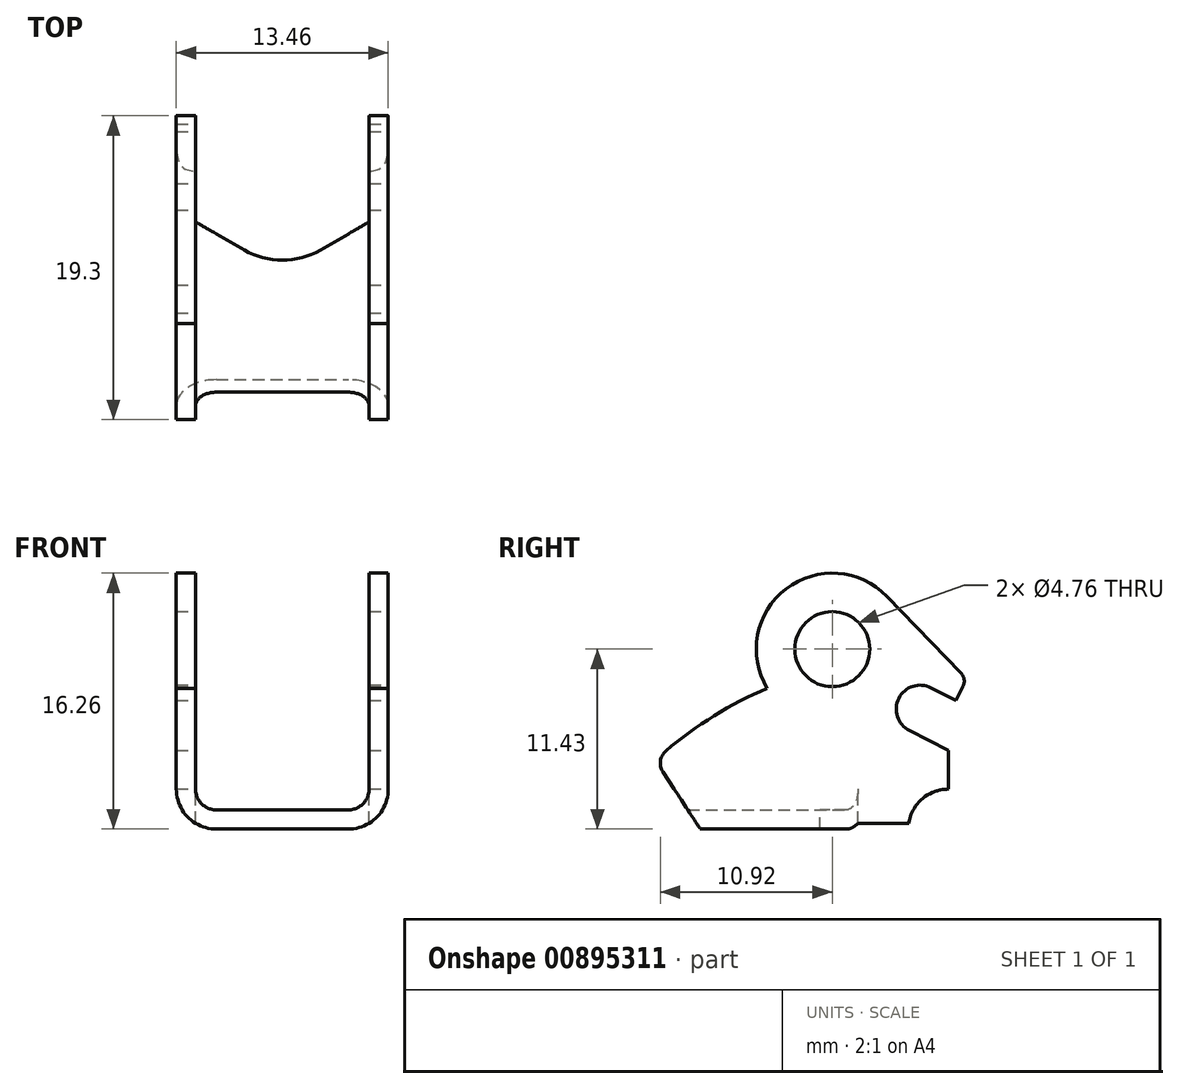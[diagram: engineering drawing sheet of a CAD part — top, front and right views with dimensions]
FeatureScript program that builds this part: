
annotation { "Feature Type Name" : "Feature", "Feature Type Description" : "" }
export const myFeature = defineFeature(function(context is Context, id is Id, definition is map)
    precondition{}
    {
        {
            var Q0;
            Q0=qCreatedBy(makeId("Front.planeOp"),FACE);
            var sketch = newSketch(context, id + "F0", { "sketchPlane" : qUnion([Q0])});
            skLineSegment(sketch, "E0.top", {"start": v(-4.2, 0) * mm, "end": v(4.2, 0) * mm});
            skLineSegment(sketch, "E0.left", {"start": v(-6.73, 25.4) * mm, "end": v(-6.73, 2.54) * mm});
            skLineSegment(sketch, "E0.right", {"start": v(6.73, 25.4) * mm, "end": v(6.73, 2.54) * mm});
            skPoint(sketch, "E1.visualSharp", {"position": v(-6.73, 0) * mm});
            skArc(sketch, "E1.filletArc", {"start": v(-6.73, 2.54) * mm, "mid": v(-5.99, 0.74) * mm, "end": v(-4.2, 0) * mm});
            skPoint(sketch, "E2.visualSharp", {"position": v(6.73, 0) * mm});
            skArc(sketch, "E2.filletArc", {"start": v(4.2, 0) * mm, "mid": v(5.99, 0.74) * mm, "end": v(6.73, 2.54) * mm});
            skLineSegment(sketch, "E3.0", {"start": v(5.51, 25.4) * mm, "end": v(5.51, 2.54) * mm});
            skLineSegment(sketch, "E3.1", {"start": v(-5.51, 25.4) * mm, "end": v(-5.51, 2.54) * mm});
            skArc(sketch, "E3.2", {"start": v(-5.51, 2.54) * mm, "mid": v(-5.12, 1.6) * mm, "end": v(-4.2, 1.22) * mm});
            skLineSegment(sketch, "E3.3", {"start": v(-4.2, 1.22) * mm, "end": v(4.2, 1.22) * mm});
            skArc(sketch, "E3.4", {"start": v(4.2, 1.22) * mm, "mid": v(5.12, 1.6) * mm, "end": v(5.51, 2.54) * mm});
            skLineSegment(sketch, "E4", {"start": v(-6.73, 25.4) * mm, "end": v(-5.51, 25.4) * mm});
            skLineSegment(sketch, "E5", {"start": v(5.51, 25.4) * mm, "end": v(6.73, 25.4) * mm});
            skSolve(sketch);
        }
        {
            var Q0;
            Q0 = qSketchRegion(id + "F0", true);
            extrude(context, id + "F1", {"entities" : qUnion([Q0]), "endBound" : BoundingType.SYMMETRIC, "depth" : 25.4 * mm, "offsetDistance" : 25.4 * mm});
        }
        {
            var Q0;
            Q0=qCreatedBy(makeId("Right.planeOp"),FACE);
            var sketch = newSketch(context, id + "F2", { "sketchPlane" : qUnion([Q0])});
            skLineSegment(sketch, "E6", {"start": v(-20, 11.43) * mm, "end": v(20.9, 11.43) * mm, "construction": true});
            skLineSegment(sketch, "E7", {"start": v(-9.9, 27.47) * mm, "end": v(-9.9, -7.2) * mm, "construction": true});
            skLineSegment(sketch, "E8", {"start": v(5.59, 5.39) * mm, "end": v(5.59, -18.34) * mm, "construction": true});
            skLineSegment(sketch, "E9", {"start": v(-18.82, -13.97) * mm, "end": v(26.6, -13.97) * mm, "construction": true});
            skLineSegment(sketch, "E10", {"start": v(-23.18, 4.2) * mm, "end": v(8.59, 4.2) * mm, "construction": true});
            skCircle(sketch, "E11", {"center": v(-9.9, 4.2) * mm, "radius": 1.02 * mm, "construction": true});
            skLineSegment(sketch, "E12", {"start": v(-8.38, 6.18) * mm, "end": v(-8.38, -4.98) * mm, "construction": true});
            skLineSegment(sketch, "E13", {"start": v(-8.38, 0) * mm, "end": v(-10.76, 3.64) * mm});
            skLineSegment(sketch, "E14", {"start": v(0, 15.75) * mm, "end": v(0, -4.51) * mm, "construction": true});
            skArc(sketch, "E15", {"start": v(-10.57, 4.97) * mm, "mid": v(-10.91, 4.34) * mm, "end": v(-10.76, 3.64) * mm});
            skPoint(sketch, "E16", {"position": v(-8.09, 6.83) * mm});
            skArc(sketch, "E17", {"start": v(-4.14, 8.94) * mm, "mid": v(-7.5, 7.2) * mm, "end": v(-10.57, 4.97) * mm});
            skCircle(sketch, "E18", {"center": v(0, 11.43) * mm, "radius": 2.38 * mm});
            skLineSegment(sketch, "E19", {"start": v(5.59, 15.52) * mm, "end": v(5.59, 7.4) * mm, "construction": true});
            skLineSegment(sketch, "E20", {"start": v(7.62, 15.4) * mm, "end": v(7.62, 6.54) * mm, "construction": true});
            skLineSegment(sketch, "E21", {"start": v(9.97, 9.4) * mm, "end": v(2.43, 9.4) * mm, "construction": true});
            skLineSegment(sketch, "E22", {"start": v(3.47, 14.79) * mm, "end": v(8.17, 9.93) * mm});
            skArc(sketch, "E23", {"start": v(3.47, 14.79) * mm, "mid": v(-2.94, 15.26) * mm, "end": v(-4.14, 8.94) * mm});
            skLineSegment(sketch, "E24", {"start": v(13.77, 7.62) * mm, "end": v(4.28, 7.62) * mm, "construction": true});
            skLineSegment(sketch, "E25", {"start": v(4.9, 6.26) * mm, "end": v(8.4, 4.48) * mm, "construction": true});
            skArc(sketch, "E26", {"start": v(8.3, 9.05) * mm, "mid": v(8.37, 9.51) * mm, "end": v(8.17, 9.93) * mm});
            skLineSegment(sketch, "E27", {"start": v(8.3, 9.05) * mm, "end": v(7.85, 8.18) * mm});
            skLineSegment(sketch, "E28", {"start": v(7.85, 8.18) * mm, "end": v(6.28, 8.98) * mm});
            skArc(sketch, "E29", {"start": v(6.28, 8.98) * mm, "mid": v(4.23, 8.31) * mm, "end": v(4.9, 6.26) * mm});
            skLineSegment(sketch, "E30", {"start": v(4.9, 6.26) * mm, "end": v(7.37, 5) * mm});
            skLineSegment(sketch, "E31", {"start": v(14.66, 2.54) * mm, "end": v(3.5, 2.54) * mm, "construction": true});
            skLineSegment(sketch, "E32", {"start": v(7.37, 5) * mm, "end": v(7.37, 2.54) * mm, "construction": true});
            skArc(sketch, "E33", {"start": v(7.37, 2.54) * mm, "mid": v(5.57, 1.8) * mm, "end": v(4.83, 0) * mm});
            skLineSegment(sketch, "E34", {"start": v(7.37, 5) * mm, "end": v(7.37, 2.54) * mm});
            skLineSegment(sketch, "E35", {"start": v(4.83, 0) * mm, "end": v(-8.38, 0) * mm});
            skSolve(sketch);
        }
        {
            var Q0;
            Q0 = qSketchRegion(id + "F2", true);
            extrude(context, id + "F3", {"entities" : qUnion([Q0]), "operationType" : NewBodyOperationType.INTERSECT, "endBound" : BoundingType.SYMMETRIC, "oppositeDirection" : true, "depth" : 50.8 * mm, "offsetDistance" : 25.4 * mm});
        }
        {
            var Q0;
            Q0=qCreatedBy(makeId("Top.planeOp"),FACE);
            var sketch = newSketch(context, id + "F4", { "sketchPlane" : qUnion([Q0])});
            skLineSegment(sketch, "E36.0", {"start": v(4.2, -9.18) * mm, "end": v(-4.2, -9.18) * mm, "construction": true});
            skLineSegment(sketch, "E37", {"start": v(-9.3, -0.8) * mm, "end": v(11.54, -0.8) * mm, "construction": true});
            skCircle(sketch, "E38", {"center": v(0, 4.03) * mm, "radius": 4.83 * mm, "construction": true});
            skLineSegment(sketch, "E39", {"start": v(10.52, 4.53) * mm, "end": v(-1.79, -2.57) * mm, "construction": true});
            skLineSegment(sketch, "E40", {"start": v(-8, 3.08) * mm, "end": v(2.5, -2.99) * mm});
            skLineSegment(sketch, "E41.0", {"start": v(5.51, 3.47) * mm, "end": v(5.51, -4.83) * mm});
            skLineSegment(sketch, "E41.1", {"start": v(-5.51, 3.47) * mm, "end": v(-5.51, -4.83) * mm});
            skLineSegment(sketch, "E42", {"start": v(-5.51, 1.64) * mm, "end": v(-2.67, 0) * mm});
            skLineSegment(sketch, "E43", {"start": v(5.51, 1.64) * mm, "end": v(5.51, 11.05) * mm});
            skLineSegment(sketch, "E44", {"start": v(5.51, 11.05) * mm, "end": v(-5.51, 11.05) * mm});
            skLineSegment(sketch, "E45", {"start": v(-5.51, 11.05) * mm, "end": v(-5.51, 1.64) * mm});
            skLineSegment(sketch, "E46", {"start": v(5.51, 1.64) * mm, "end": v(2.41, -0.15) * mm});
            skArc(sketch, "E47", {"start": v(-2.65, 0) * mm, "mid": v(-0.14, -0.8) * mm, "end": v(2.41, -0.15) * mm});
            skSolve(sketch);
        }
        {
            var Q0;
            Q0 = qSketchRegion(id + "F4", true);
            extrude(context, id + "F5", {"entities" : qUnion([Q0]), "operationType" : NewBodyOperationType.REMOVE, "endBound" : BoundingType.SYMMETRIC, "oppositeDirection" : true, "depth" : 25.4 * mm, "offsetDistance" : 25.4 * mm});
        }
    });
